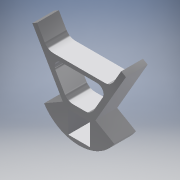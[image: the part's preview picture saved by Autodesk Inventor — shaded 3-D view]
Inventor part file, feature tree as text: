
AUTODESK INVENTOR PART (.ipt)
format: ipt  version: 2016 (Build 200138000, 138)  size: 166,400 bytes
history: native  units: in
note: dims shown in document units (in); Inventor stores cm internally (conversion verified against a paired STEP export)
features: other x3, extrude x2, sketch x1
ambient origin geometry x8: Origin, YZ Plane, XZ Plane, XY Plane, X Axis, Y Axis, Z Axis, Center Point
bodies: Body1 (feature_tree)
feature tree (6):
  other  "Table"
  other  "vertex-top"
  other  "vertex-bottom"
  sketch  "Sketch1"  dims[d12=1.1811in d13=0.5906in d15=0.7874in d16=0.7874in d20=2.2047in d21=2.2047in d22=0.7874in d23=0.7874in d24=0.3937in d31=0.5906in d33=3.0315in d34=1.1811in d36=0.0in d37=1.1024in d38=0.1969in d39=0.1969in d40=0.1417in d41=0.374in d42=0.3543in d43=0.2362in d44=0.3937in d45=0.0in]
  extrude  "Extrusion2"  Depth=0.3937in
  extrude  "Extrusion3"  Depth=0.7874in
